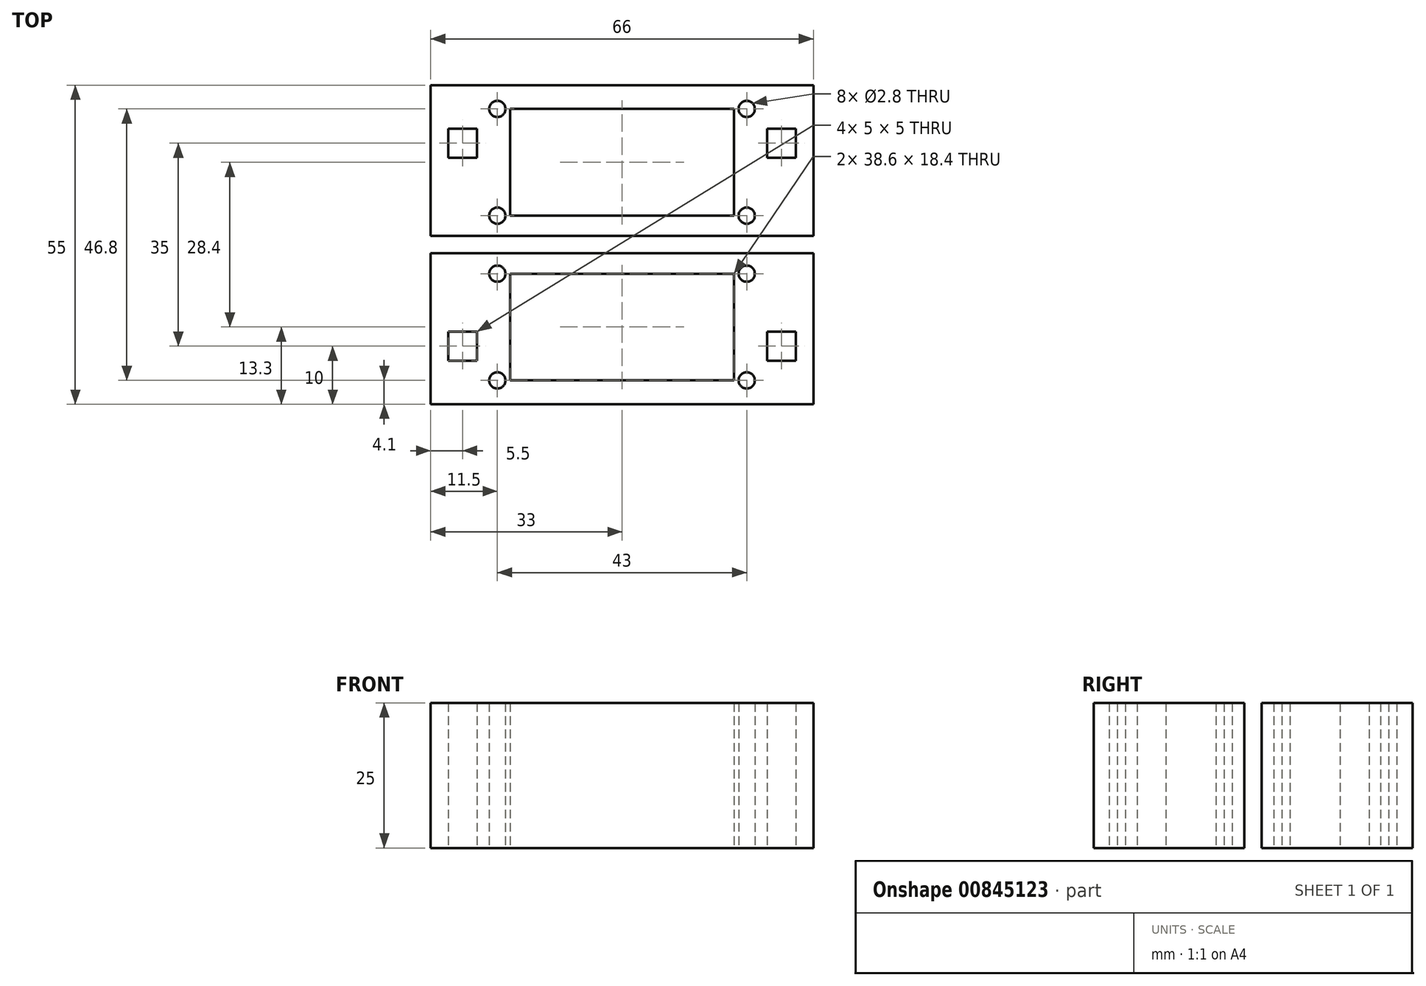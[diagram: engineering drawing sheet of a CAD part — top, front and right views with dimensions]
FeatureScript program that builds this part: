
annotation { "Feature Type Name" : "Feature", "Feature Type Description" : "" }
export const myFeature = defineFeature(function(context is Context, id is Id, definition is map)
    precondition{}
    {
        {
            var Q0;
            Q0=qCreatedBy(makeId("Top.planeOp"),FACE);
            var sketch = newSketch(context, id + "F0", { "sketchPlane" : qUnion([Q0])});
            skLineSegment(sketch, "E0.bottom", {"start": v(33, 27.5) * mm, "end": v(-33, 27.5) * mm});
            skLineSegment(sketch, "E0.top", {"start": v(33, -27.5) * mm, "end": v(-33, -27.5) * mm});
            skLineSegment(sketch, "E0.left", {"start": v(33, 27.5) * mm, "end": v(33, -27.5) * mm});
            skLineSegment(sketch, "E0.right", {"start": v(-33, 27.5) * mm, "end": v(-33, -27.5) * mm});
            skPoint(sketch, "E0.middle", {"position": v(0, 0) * mm});
            skLineSegment(sketch, "E1.bottom", {"start": v(25, -15) * mm, "end": v(-25, -15) * mm, "construction": true});
            skLineSegment(sketch, "E1.top", {"start": v(25, 15) * mm, "end": v(-25, 15) * mm, "construction": true});
            skLineSegment(sketch, "E1.left", {"start": v(25, -15) * mm, "end": v(25, 15) * mm, "construction": true});
            skLineSegment(sketch, "E1.right", {"start": v(-25, -15) * mm, "end": v(-25, 15) * mm, "construction": true});
            skLineSegment(sketch, "E2.bottom", {"start": v(-30, 20) * mm, "end": v(30, 20) * mm, "construction": true});
            skLineSegment(sketch, "E2.top", {"start": v(-30, -20) * mm, "end": v(30, -20) * mm, "construction": true});
            skLineSegment(sketch, "E2.left", {"start": v(-30, 20) * mm, "end": v(-30, -20) * mm, "construction": true});
            skLineSegment(sketch, "E2.right", {"start": v(30, 20) * mm, "end": v(30, -20) * mm, "construction": true});
            skLineSegment(sketch, "E3.bottom", {"start": v(-25, 15) * mm, "end": v(-30, 15) * mm});
            skLineSegment(sketch, "E3.top", {"start": v(-25, 20) * mm, "end": v(-30, 20) * mm});
            skLineSegment(sketch, "E3.left", {"start": v(-25, 15) * mm, "end": v(-25, 20) * mm});
            skLineSegment(sketch, "E3.right", {"start": v(-30, 15) * mm, "end": v(-30, 20) * mm});
            skLineSegment(sketch, "E4.bottom", {"start": v(25, 15) * mm, "end": v(30, 15) * mm});
            skLineSegment(sketch, "E4.top", {"start": v(25, 20) * mm, "end": v(30, 20) * mm});
            skLineSegment(sketch, "E4.left", {"start": v(25, 15) * mm, "end": v(25, 20) * mm});
            skLineSegment(sketch, "E4.right", {"start": v(30, 15) * mm, "end": v(30, 20) * mm});
            skLineSegment(sketch, "E5.bottom", {"start": v(25, -15) * mm, "end": v(30, -15) * mm});
            skLineSegment(sketch, "E5.top", {"start": v(25, -20) * mm, "end": v(30, -20) * mm});
            skLineSegment(sketch, "E5.left", {"start": v(25, -15) * mm, "end": v(25, -20) * mm});
            skLineSegment(sketch, "E5.right", {"start": v(30, -15) * mm, "end": v(30, -20) * mm});
            skLineSegment(sketch, "E6.bottom", {"start": v(-25, -15) * mm, "end": v(-30, -15) * mm});
            skLineSegment(sketch, "E6.top", {"start": v(-25, -20) * mm, "end": v(-30, -20) * mm});
            skLineSegment(sketch, "E6.left", {"start": v(-25, -15) * mm, "end": v(-25, -20) * mm});
            skLineSegment(sketch, "E6.right", {"start": v(-30, -15) * mm, "end": v(-30, -20) * mm});
            skLineSegment(sketch, "E7.bottom", {"start": v(19.3, 5) * mm, "end": v(-19.3, 5) * mm});
            skLineSegment(sketch, "E7.top", {"start": v(19.3, 23.4) * mm, "end": v(-19.3, 23.4) * mm});
            skLineSegment(sketch, "E7.left", {"start": v(19.3, 5) * mm, "end": v(19.3, 23.4) * mm});
            skLineSegment(sketch, "E7.right", {"start": v(-19.3, 5) * mm, "end": v(-19.3, 23.4) * mm});
            skPoint(sketch, "E7.middle", {"position": v(0, 14.2) * mm});
            skLineSegment(sketch, "E8.bottom", {"start": v(19.3, -23.4) * mm, "end": v(-19.3, -23.4) * mm});
            skLineSegment(sketch, "E8.top", {"start": v(19.3, -5) * mm, "end": v(-19.3, -5) * mm});
            skLineSegment(sketch, "E8.left", {"start": v(19.3, -23.4) * mm, "end": v(19.3, -5) * mm});
            skLineSegment(sketch, "E8.right", {"start": v(-19.3, -23.4) * mm, "end": v(-19.3, -5) * mm});
            skPoint(sketch, "E8.middle", {"position": v(0, -14.2) * mm});
            skLineSegment(sketch, "E9.bottom", {"start": v(21.5, 23.4) * mm, "end": v(-21.5, 23.4) * mm, "construction": true});
            skLineSegment(sketch, "E9.top", {"start": v(21.5, -23.4) * mm, "end": v(-21.5, -23.4) * mm, "construction": true});
            skLineSegment(sketch, "E9.left", {"start": v(21.5, 23.4) * mm, "end": v(21.5, -23.4) * mm, "construction": true});
            skLineSegment(sketch, "E9.right", {"start": v(-21.5, 23.4) * mm, "end": v(-21.5, -23.4) * mm, "construction": true});
            skLineSegment(sketch, "E10.bottom", {"start": v(-21.5, -23.4) * mm, "end": v(21.5, -23.4) * mm, "construction": true});
            skLineSegment(sketch, "E10.top", {"start": v(-21.5, -5) * mm, "end": v(21.5, -5) * mm, "construction": true});
            skLineSegment(sketch, "E10.left", {"start": v(-21.5, -23.4) * mm, "end": v(-21.5, -5) * mm, "construction": true});
            skLineSegment(sketch, "E10.right", {"start": v(21.5, -23.4) * mm, "end": v(21.5, -5) * mm, "construction": true});
            skLineSegment(sketch, "E11.top", {"start": v(21.5, 5) * mm, "end": v(-21.5, 5) * mm, "construction": true});
            skLineSegment(sketch, "E11.left", {"start": v(21.5, 23.4) * mm, "end": v(21.5, 5) * mm, "construction": true});
            skLineSegment(sketch, "E11.right", {"start": v(-21.5, 23.4) * mm, "end": v(-21.5, 5) * mm, "construction": true});
            skCircle(sketch, "E12", {"center": v(-21.5, -23.4) * mm, "radius": 1.4 * mm});
            skCircle(sketch, "E13", {"center": v(21.5, -23.4) * mm, "radius": 1.4 * mm});
            skCircle(sketch, "E14", {"center": v(21.5, -5) * mm, "radius": 1.4 * mm});
            skCircle(sketch, "E15", {"center": v(-21.5, -5) * mm, "radius": 1.4 * mm});
            skCircle(sketch, "E16", {"center": v(-21.5, 5) * mm, "radius": 1.4 * mm});
            skCircle(sketch, "E17", {"center": v(21.5, 5) * mm, "radius": 1.4 * mm});
            skCircle(sketch, "E18", {"center": v(-21.5, 23.4) * mm, "radius": 1.4 * mm});
            skCircle(sketch, "E19", {"center": v(21.5, 23.4) * mm, "radius": 1.4 * mm});
            skSolve(sketch);
        }
        {
            var Q0;
            Q0 = qSketchRegion(id + "F0", true);
            extrude(context, id + "F1", {"entities" : qUnion([Q0]), "depth" : 25 * mm, "offsetDistance" : 25 * mm});
        }
        {
            var Q0;
            Q0=makeQuery(id+"F1.opExtrude","CAP_FACE",FACE,{"disambiguationData":[OSD([sQuery(id+"F0.wireOp",EDGE,"E0.bottom"),sQuery(id+"F0.wireOp",EDGE,"E0.top"),sQuery(id+"F0.wireOp",EDGE,"E0.left"),sQuery(id+"F0.wireOp",EDGE,"E0.right"),sQuery(id+"F0.wireOp",EDGE,"E3.bottom"),sQuery(id+"F0.wireOp",EDGE,"E3.top"),sQuery(id+"F0.wireOp",EDGE,"E3.left"),sQuery(id+"F0.wireOp",EDGE,"E3.right"),sQuery(id+"F0.wireOp",EDGE,"E4.bottom"),sQuery(id+"F0.wireOp",EDGE,"E4.top"),sQuery(id+"F0.wireOp",EDGE,"E4.left"),sQuery(id+"F0.wireOp",EDGE,"E4.right"),sQuery(id+"F0.wireOp",EDGE,"E5.bottom"),sQuery(id+"F0.wireOp",EDGE,"E5.top"),sQuery(id+"F0.wireOp",EDGE,"E5.left"),sQuery(id+"F0.wireOp",EDGE,"E5.right"),sQuery(id+"F0.wireOp",EDGE,"E6.bottom"),sQuery(id+"F0.wireOp",EDGE,"E6.top"),sQuery(id+"F0.wireOp",EDGE,"E6.left"),sQuery(id+"F0.wireOp",EDGE,"E6.right"),sQuery(id+"F0.wireOp",EDGE,"E7.bottom"),sQuery(id+"F0.wireOp",EDGE,"E7.top"),sQuery(id+"F0.wireOp",EDGE,"E7.left"),sQuery(id+"F0.wireOp",EDGE,"E7.right"),sQuery(id+"F0.wireOp",EDGE,"E8.bottom"),sQuery(id+"F0.wireOp",EDGE,"E8.top"),sQuery(id+"F0.wireOp",EDGE,"E8.left"),sQuery(id+"F0.wireOp",EDGE,"E8.right")])],"isStart":false});
            var sketch = newSketch(context, id + "F2", { "sketchPlane" : qUnion([Q0])});
            skLineSegment(sketch, "E20.bottom", {"start": v(-33, 1.5) * mm, "end": v(33, 1.5) * mm});
            skLineSegment(sketch, "E20.top", {"start": v(-33, -1.5) * mm, "end": v(33, -1.5) * mm});
            skLineSegment(sketch, "E20.left", {"start": v(-33, 1.5) * mm, "end": v(-33, -1.5) * mm});
            skLineSegment(sketch, "E20.right", {"start": v(33, 1.5) * mm, "end": v(33, -1.5) * mm});
            skSolve(sketch);
        }
        {
            var Q0;
            Q0 = qSketchRegion(id + "F2", true);
            extrude(context, id + "F3", {"entities" : qUnion([Q0]), "operationType" : NewBodyOperationType.REMOVE, "oppositeDirection" : true, "depth" : 25 * mm, "offsetDistance" : 25 * mm});
        }
    });
